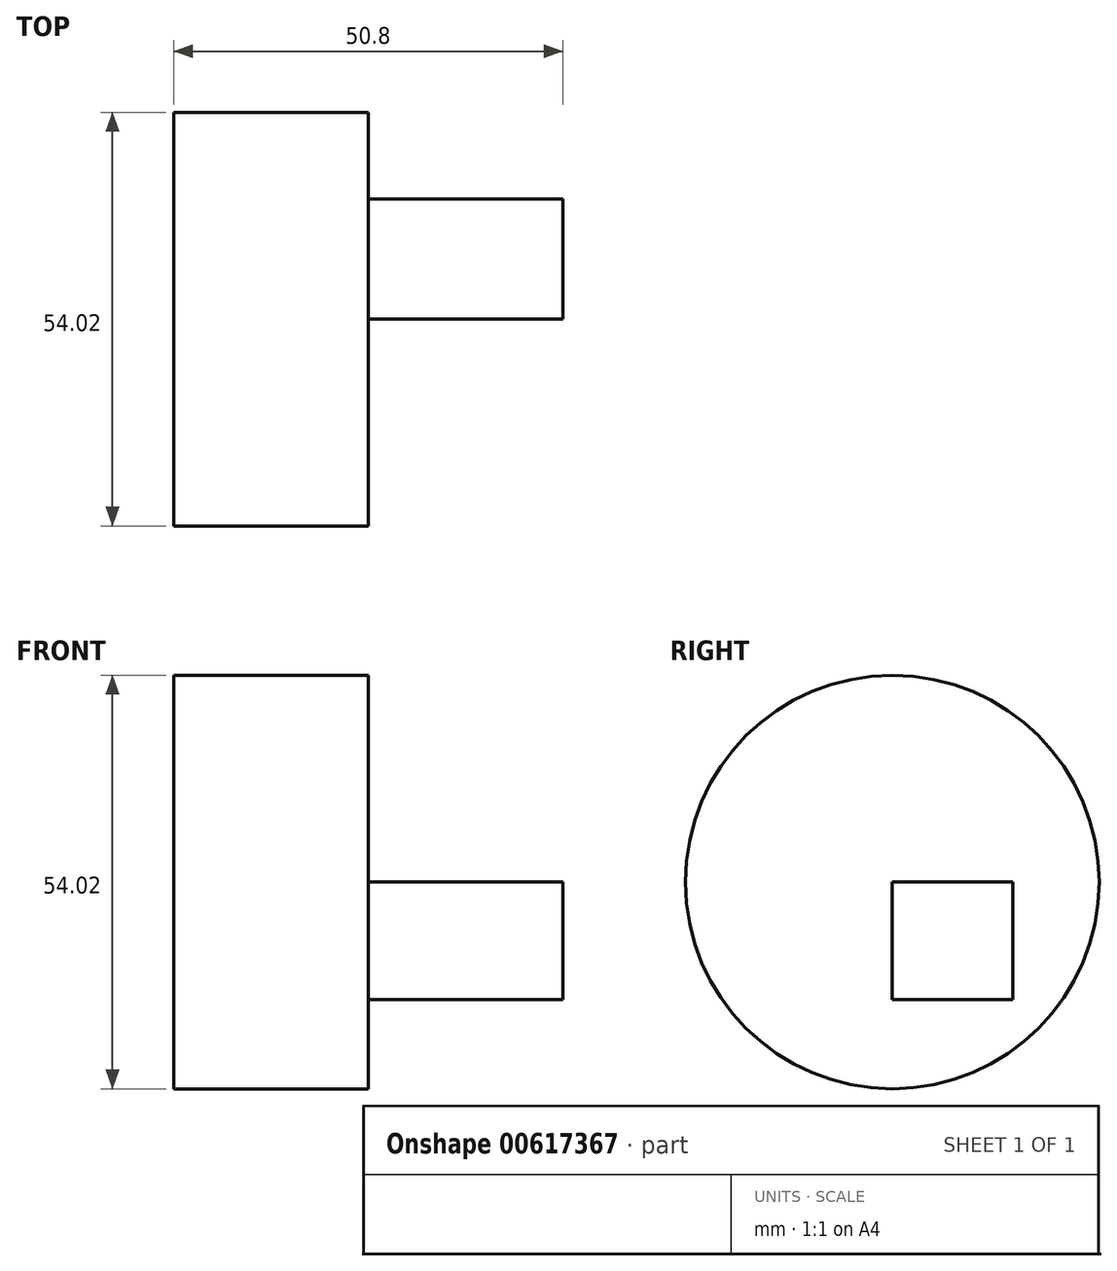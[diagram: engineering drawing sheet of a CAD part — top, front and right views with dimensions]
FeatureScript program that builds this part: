
annotation { "Feature Type Name" : "Feature", "Feature Type Description" : "" }
export const myFeature = defineFeature(function(context is Context, id is Id, definition is map)
    precondition{}
    {
        {
            var Q0;
            Q0=qCreatedBy(makeId("Right.planeOp"),FACE);
            var sketch = newSketch(context, id + "F0", { "sketchPlane" : qUnion([Q0])});
            skCircle(sketch, "E0", {"center": v(0, 0) * mm, "radius": 27 * mm});
            skSolve(sketch);
        }
        {
            var Q0;
            Q0=makeQuery(id+"F0.imprint","IMPRINT",FACE,{"disambiguationData":[TD([[makeQuery(id+"F0.imprint","IMPRINT",EDGE,{"derivedFrom":sQuery(id+"F0.wireOp",EDGE,"E0")}),1.0]])]});
            extrude(context, id + "F1", {"entities" : qUnion([Q0]), "depth" : 25.4 * mm, "offsetDistance" : 25.4 * mm});
        }
        {
            var Q0;
            Q0=makeQuery(id+"F1.opExtrude","CAP_FACE",FACE,{"disambiguationData":[OSD([sQuery(id+"F0.wireOp",EDGE,"E0")])],"isStart":false});
            var sketch = newSketch(context, id + "F2", { "sketchPlane" : qUnion([Q0])});
            skLineSegment(sketch, "E1.bottom", {"start": v(0, 0) * mm, "end": v(15.73, 0) * mm});
            skLineSegment(sketch, "E1.top", {"start": v(0, -15.33) * mm, "end": v(15.73, -15.33) * mm});
            skLineSegment(sketch, "E1.left", {"start": v(0, 0) * mm, "end": v(0, -15.33) * mm});
            skLineSegment(sketch, "E1.right", {"start": v(15.73, 0) * mm, "end": v(15.73, -15.33) * mm});
            skSolve(sketch);
        }
        {
            var Q0;
            Q0=makeQuery(id+"F2.imprint","IMPRINT",FACE,{"disambiguationData":[TD([[makeQuery(id+"F2.imprint","IMPRINT",EDGE,{"derivedFrom":sQuery(id+"F2.wireOp",EDGE,"E1.bottom")}),-1.0]])]});
            extrude(context, id + "F3", {"entities" : qUnion([Q0]), "operationType" : NewBodyOperationType.ADD, "depth" : 25.4 * mm, "offsetDistance" : 25.4 * mm});
        }
    });
